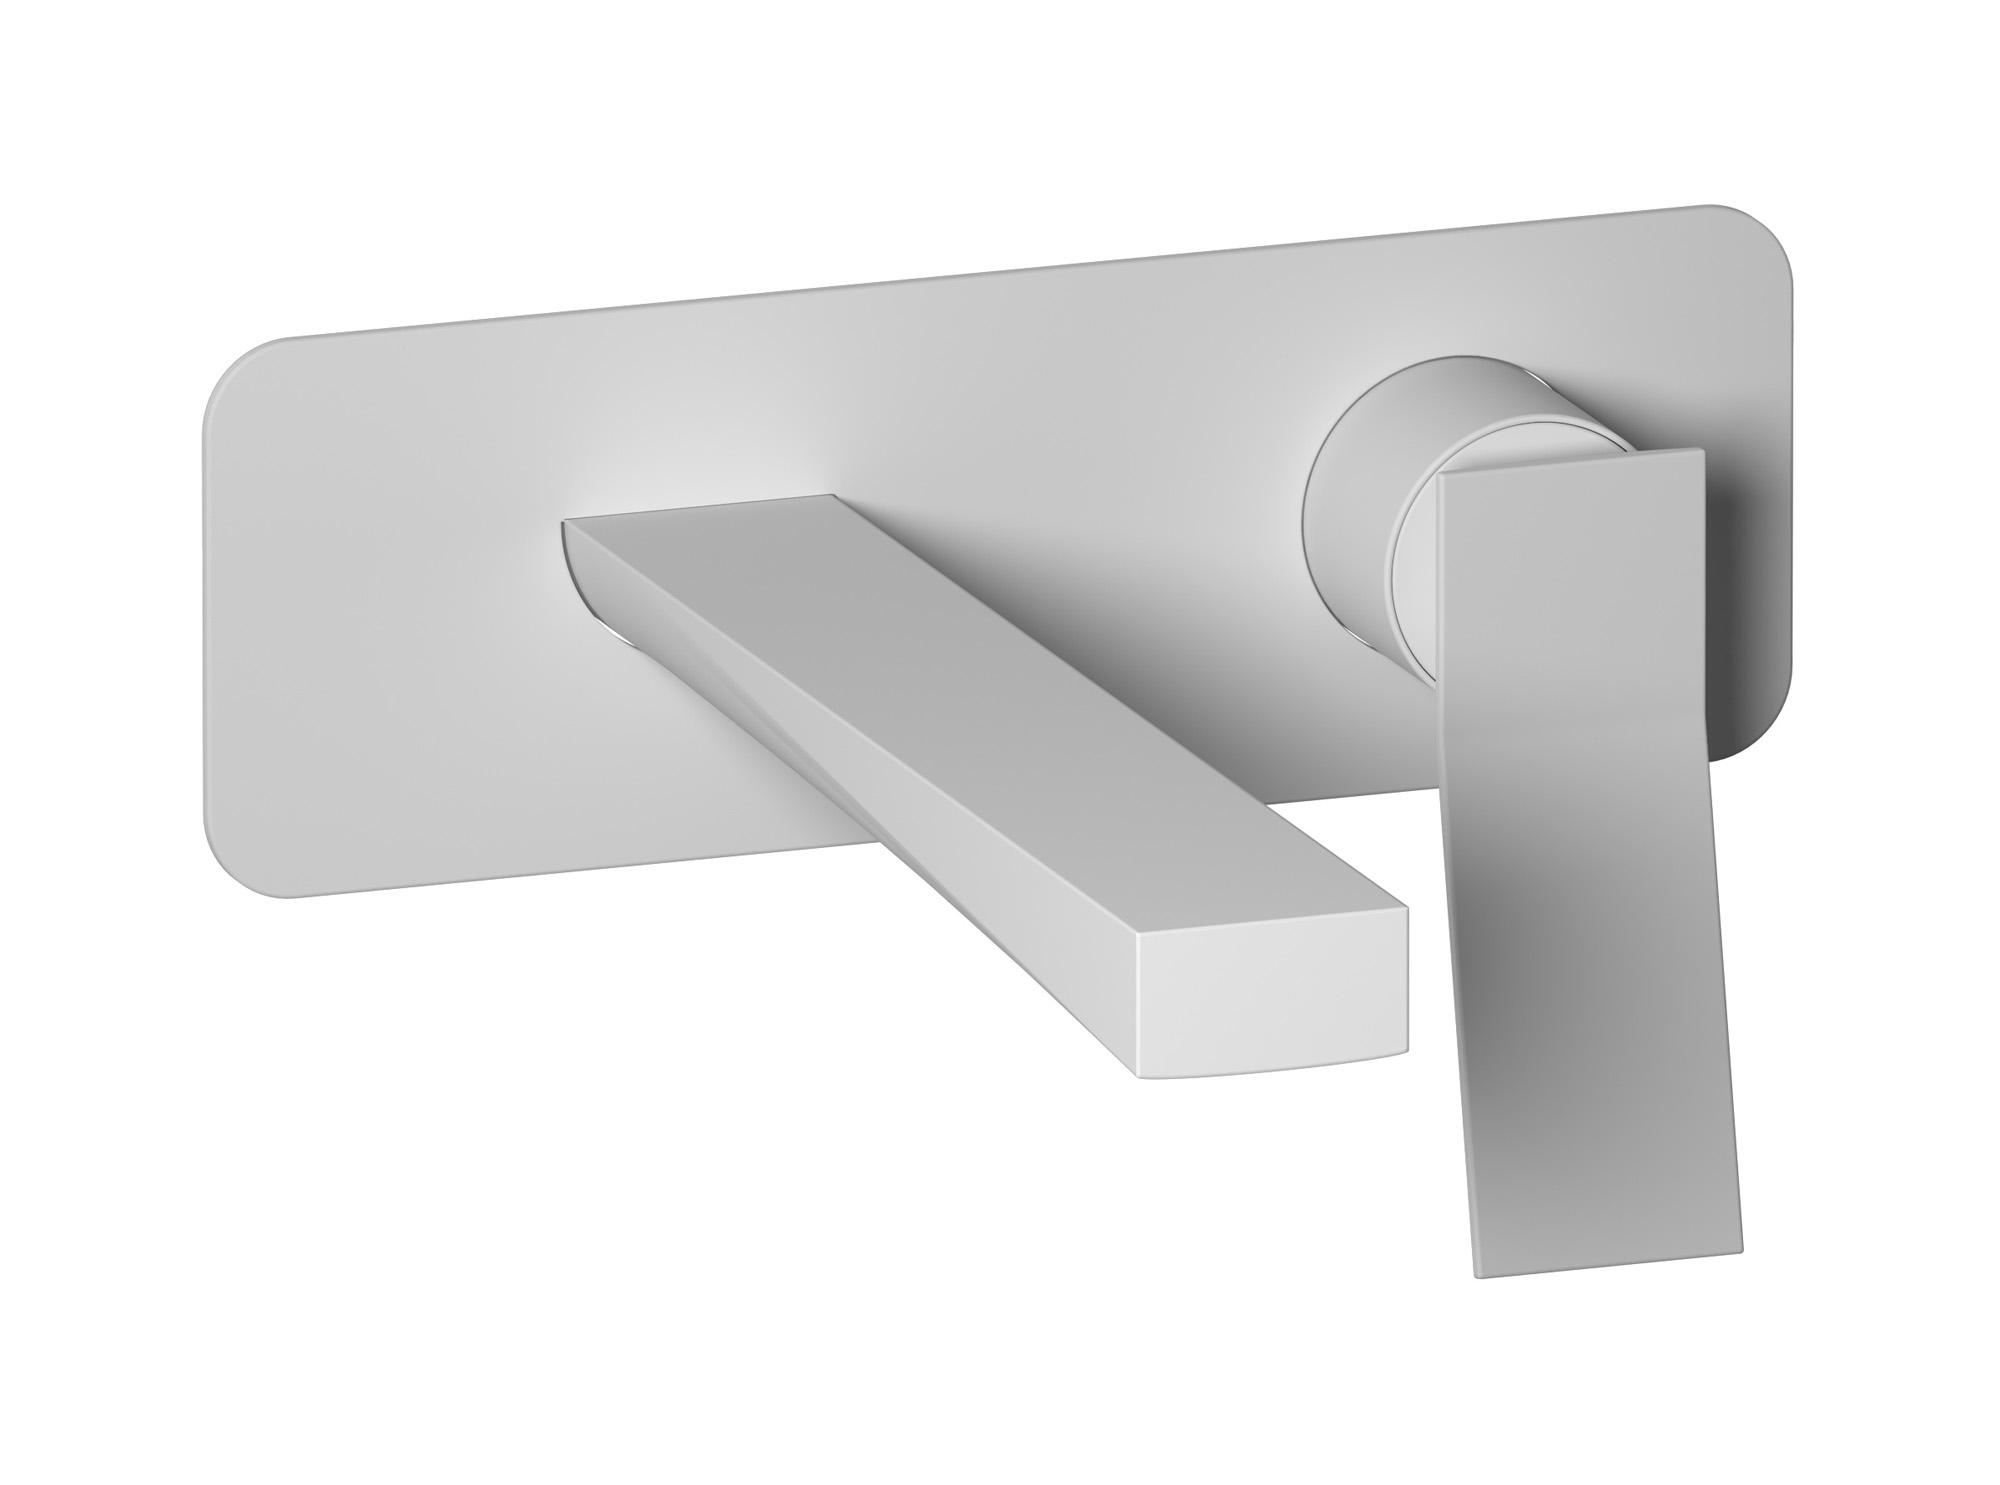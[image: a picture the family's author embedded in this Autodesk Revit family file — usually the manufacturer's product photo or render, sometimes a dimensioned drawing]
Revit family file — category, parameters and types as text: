
# Revit family: WA206
name_source: partatom
category: Apparecchi idraulici
units: mm (PartAtom-declared; Revit-internal decimal feet)

## family parameters
Basato su piano di lavoro = No
Condiviso = No
Mantieni orientamento annotazione = No
Numero OmniClass = 23.45.55.17
Punto di calcolo locali = No
Quota connettore circolare = Usa diametro
Sempre verticale = Sì
Taglio con vuoti quando caricato = No
Tipo di parte = Normale
Titolo OmniClass = Mixing Faucets

## types (12) — shared parameters
Cold water inlet = 10 mm  [stored 0.0328084 ft]
Commenti sul tipo = Washbasin mixer
Connessione CW = No
Connessione HW = No
Connessione di scarico = No
Connessione di ventilazione = No
Descrizione = Wall mounted washbasin mixer complete with drain
Hot water inlet = 10 mm  [stored 0.0328084 ft]
Produttore = IB Rubinetterie S.p.A.
URL = https://www.weareib.it
zero-valued in all types: Prospetto di default

## per-type parameters (varying)
| type | Finishes surface | Immagine tipo | Modello |
| Chrome | IB_Chrome | WA206CC.jpg | WA206CC |
| Brushed nickel | IB_Chrome | WA206SS.jpg | WA206SS |
| Matt black | IB_matt black | WA206NP.jpg | WA206NP |
| Matt white | IB_matt white | WA206BO.jpg | WA206BO |
| Black chrome | IB_Black chrome | WA206CF.jpg | WA206CF |
| Brushed black chrome | IB_Brushed black chrome | WA206CS.jpg | WA206CS |
| Pale gold | IB_Pale gold | WA206II.jpg | WA206II |
| Brushed pale gold | IB_brushed pale gold | WA206IS.jpg | WA206IS |
| Rose gold | IB_Rose gold | WA206RS.jpg | WA206RS |
| Brushed rose gold | IB_Brushed rose gold | WA206SR.jpg | WA206SR |
| Gold | IB_gold | WA206OO.jpg | WA206OO |
| Brushed gold | IB_brushed gold | WA206OS.jpg | WA206OS |

note: [stored X ft] marks values corroborated as IEEE doubles in the binary element streams (Revit-internal decimal feet)
